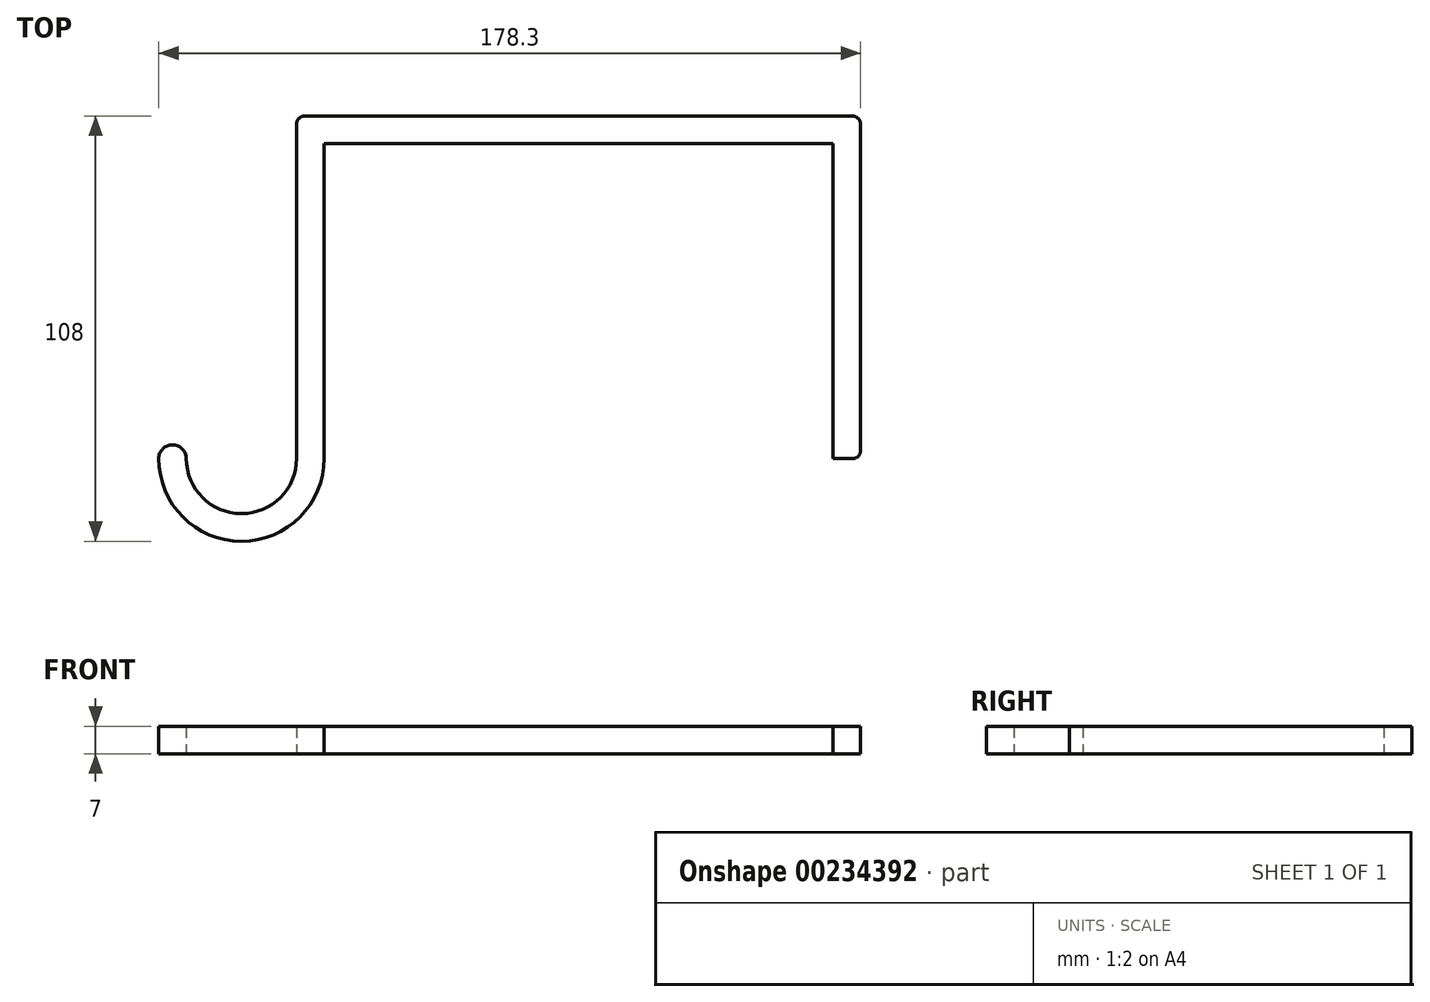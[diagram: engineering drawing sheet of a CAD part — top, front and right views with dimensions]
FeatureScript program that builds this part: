
annotation { "Feature Type Name" : "Feature", "Feature Type Description" : "" }
export const myFeature = defineFeature(function(context is Context, id is Id, definition is map)
    precondition{}
    {
        {
            assignVariable(context, id + "F0", {"name" : "D", "anyValue" : 7});
        }
        {
            var Q0;
            Q0=qCreatedBy(makeId("Top.planeOp"),FACE);
            var sketch = newSketch(context, id + "F1", { "sketchPlane" : qUnion([Q0])});
            skArc(sketch, "E0", {"start": v(-14, 0) * mm, "mid": v(0, -14) * mm, "end": v(14, 0) * mm});
            skLineSegment(sketch, "E1", {"start": v(14, 0) * mm, "end": v(14, 85) * mm});
            skLineSegment(sketch, "E2", {"start": v(16, 87) * mm, "end": v(155.3, 87) * mm});
            skLineSegment(sketch, "E3", {"start": v(157.3, 85) * mm, "end": v(157.3, 2) * mm});
            skLineSegment(sketch, "E4", {"start": v(155.3, 0) * mm, "end": v(150.3, 0) * mm});
            skLineSegment(sketch, "E5", {"start": v(150.3, 0) * mm, "end": v(150.3, 80) * mm});
            skLineSegment(sketch, "E6", {"start": v(150.3, 80) * mm, "end": v(21, 80) * mm});
            skLineSegment(sketch, "E7", {"start": v(21, 80) * mm, "end": v(21, 0) * mm});
            skArc(sketch, "E8", {"start": v(21, 0) * mm, "mid": v(0, -21) * mm, "end": v(-21, 0) * mm});
            skArc(sketch, "E9", {"start": v(-21, 0) * mm, "mid": v(-17.5, 3.5) * mm, "end": v(-14, 0) * mm});
            skPoint(sketch, "E10.visualSharp", {"position": v(14, 87) * mm});
            skArc(sketch, "E10.filletArc", {"start": v(16, 87) * mm, "mid": v(14.59, 86.41) * mm, "end": v(14, 85) * mm});
            skPoint(sketch, "E11.visualSharp", {"position": v(157.3, 87) * mm});
            skArc(sketch, "E11.filletArc", {"start": v(157.3, 85) * mm, "mid": v(156.71, 86.41) * mm, "end": v(155.3, 87) * mm});
            skPoint(sketch, "E12.visualSharp", {"position": v(157.3, 0) * mm});
            skArc(sketch, "E12.filletArc", {"start": v(155.3, 0) * mm, "mid": v(156.71, 0.59) * mm, "end": v(157.3, 2) * mm});
            skSolve(sketch);
        }
        {
            var Q0;
            Q0=makeQuery(id+"F1.imprint","IMPRINT",FACE,{"disambiguationData":[TD([[makeQuery(id+"F1.imprint","IMPRINT",EDGE,{"derivedFrom":sQuery(id+"F1.wireOp",EDGE,"E0")}),-1.0]])]});
            extrude(context, id + "F2", {"entities" : qUnion([Q0]), "depth" : getVariable(context, 'D') * mm});
        }
    });
